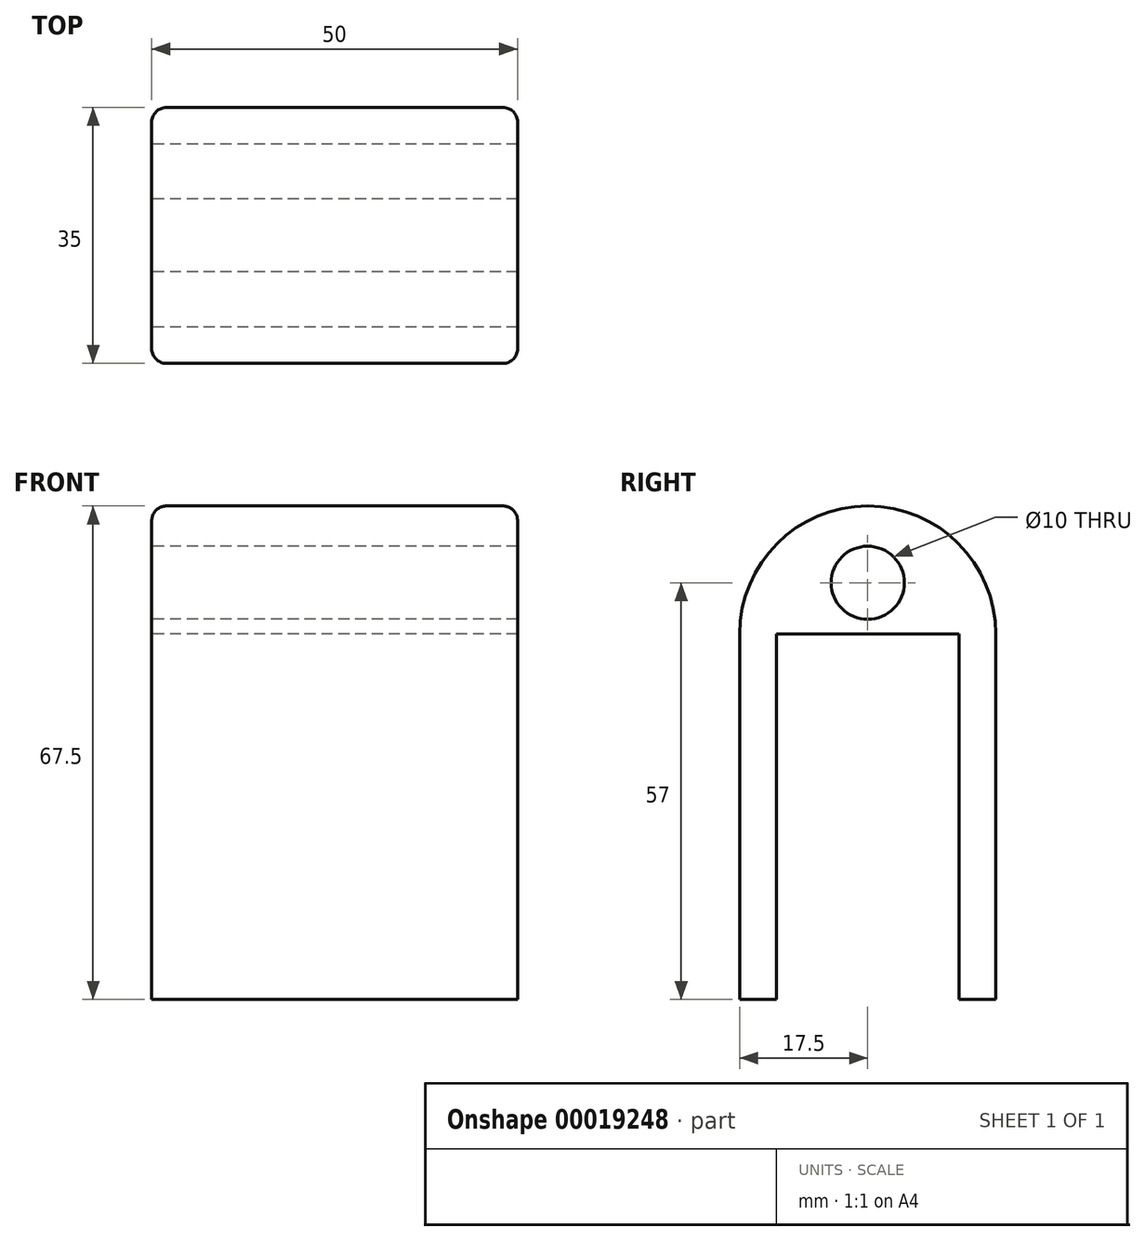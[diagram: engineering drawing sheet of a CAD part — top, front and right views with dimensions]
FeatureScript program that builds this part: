
annotation { "Feature Type Name" : "Feature", "Feature Type Description" : "" }
export const myFeature = defineFeature(function(context is Context, id is Id, definition is map)
    precondition{}
    {
        {
            var Q0;
            Q0=qCreatedBy(makeId("Right.planeOp"),FACE);
            var sketch = newSketch(context, id + "F0", { "sketchPlane" : qUnion([Q0])});
            skLineSegment(sketch, "E0.rect.bottom", {"start": v(12.5, 25) * mm, "end": v(-12.5, 25) * mm});
            skLineSegment(sketch, "E0.rect.top", {"start": v(17.5, -25) * mm, "end": v(12.5, -25) * mm});
            skLineSegment(sketch, "E0.rect.left", {"start": v(17.5, 25) * mm, "end": v(17.5, -25) * mm});
            skLineSegment(sketch, "E0.rect.right", {"start": v(-17.5, 25) * mm, "end": v(-17.5, -25) * mm});
            skPoint(sketch, "E0.rect.middle", {"position": v(0, 0) * mm});
            skLineSegment(sketch, "E1.rect.left", {"start": v(12.5, -25) * mm, "end": v(12.5, 25) * mm});
            skLineSegment(sketch, "E1.rect.right", {"start": v(-12.5, -25) * mm, "end": v(-12.5, 25) * mm});
            skArc(sketch, "E2", {"start": v(17.5, 25) * mm, "mid": v(0, 42.5) * mm, "end": v(-17.5, 25) * mm});
            skLineSegment(sketch, "E3.trimOffspring", {"start": v(-12.5, -25) * mm, "end": v(-17.5, -25) * mm});
            skSolve(sketch);
        }
        {
            var Q0;
            Q0=qCreatedBy(makeId("Right.planeOp"),FACE);
            var sketch = newSketch(context, id + "F1", { "sketchPlane" : qUnion([Q0])});
            skCircle(sketch, "E4", {"center": v(0, 32) * mm, "radius": 5 * mm});
            skSolve(sketch);
        }
        {
            var Q0;
            Q0=makeQuery(id+"F0.imprint","IMPRINT",FACE,{"disambiguationData":[TD([[makeQuery(id+"F0.imprint","IMPRINT",EDGE,{"derivedFrom":sQuery(id+"F0.wireOp",EDGE,"E0.rect.top")}),-1.0]])]});
            extrude(context, id + "F2", {"entities" : qUnion([Q0]), "depth" : 50 * mm});
        }
        {
            var Q0;
            Q0=makeQuery(id+"F1.imprint","IMPRINT",FACE,{"disambiguationData":[TD([[makeQuery(id+"F1.imprint","IMPRINT",EDGE,{"derivedFrom":sQuery(id+"F1.wireOp",EDGE,"E4")}),1.0]])]});
            extrude(context, id + "F3", {"entities" : qUnion([Q0]), "operationType" : NewBodyOperationType.REMOVE, "endBound" : BoundingType.THROUGH_ALL, "depth" : 25 * mm});
        }
        {
            var Q0;
            Q0=makeQuery(id+"F2.opExtrude","CAP_EDGE",EDGE,{"disambiguationData":[OSD([sQuery(id+"F0.wireOp",EDGE,"E0.rect.right")])],"isStart":false});
            fillet(context, id + "F4", {"entities" : qUnion([Q0]), "radius" : 2 * mm, "tangentPropagation" : true, "allowEdgeOverflow" : false});
        }
        {
            var Q0;
            Q0=makeQuery(id+"F2.opExtrude","CAP_EDGE",EDGE,{"disambiguationData":[OSD([sQuery(id+"F0.wireOp",EDGE,"E0.rect.left")])],"isStart":true});
            fillet(context, id + "F5", {"entities" : qUnion([Q0]), "radius" : 2 * mm, "tangentPropagation" : true, "allowEdgeOverflow" : false});
        }
    });
